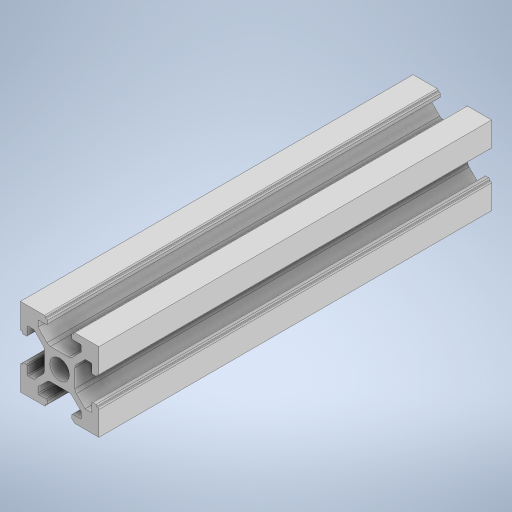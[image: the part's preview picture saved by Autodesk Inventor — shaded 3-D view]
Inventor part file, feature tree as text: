
AUTODESK INVENTOR PART (.ipt)
format: ipt  version: 2023.5 (Build 275446000, 446)  size: 363,520 bytes
history: native  units: in
note: dims shown in document units (in); Inventor stores cm internally (conversion verified against a paired STEP export)
features: extrude x1, sketch x1
ambient origin geometry x8: Origin, YZ Plane, XZ Plane, XY Plane, X Axis, Y Axis, Z Axis, Center Point
bodies: Solid1 (feature_tree)
feature tree (2):
  extrude  "Extrusion1"  Depth=3.937in TaperAngle=0.0deg
  sketch  "Sketch1"  dims[d59=0.05in d60=3.937in d61=0.0in]
